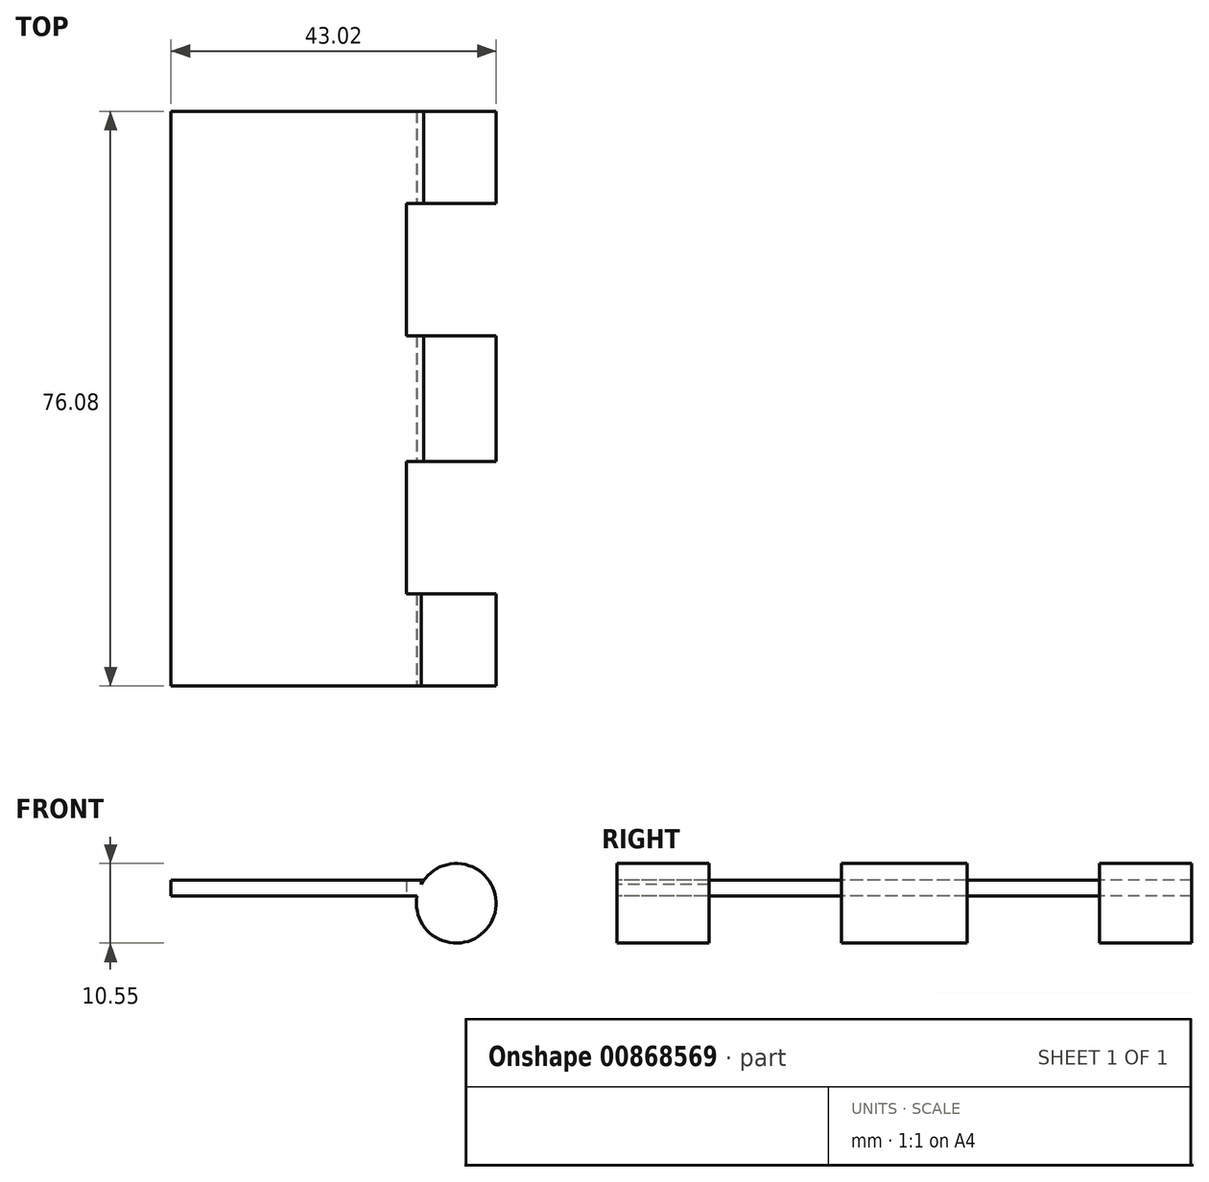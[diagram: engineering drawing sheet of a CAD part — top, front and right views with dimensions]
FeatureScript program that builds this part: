
annotation { "Feature Type Name" : "Feature", "Feature Type Description" : "" }
export const myFeature = defineFeature(function(context is Context, id is Id, definition is map)
    precondition{}
    {
        {
            var Q0;
            Q0=qCreatedBy(makeId("Top.planeOp"),FACE);
            var sketch = newSketch(context, id + "F0", { "sketchPlane" : qUnion([Q0])});
            skLineSegment(sketch, "E0.bottom", {"start": v(15.58, 38.04) * mm, "end": v(-15.58, 38.04) * mm});
            skLineSegment(sketch, "E0.top", {"start": v(15.58, -38.04) * mm, "end": v(-15.58, -38.04) * mm});
            skLineSegment(sketch, "E0.left", {"start": v(15.58, 38.04) * mm, "end": v(15.58, -38.04) * mm});
            skLineSegment(sketch, "E0.right", {"start": v(-15.58, 38.04) * mm, "end": v(-15.58, -38.04) * mm});
            skPoint(sketch, "E0.middle", {"position": v(0, 0) * mm});
            skSolve(sketch);
        }
        {
            var Q0;
            Q0=qSketchRegion(id+"F0",true);
            extrude(context, id + "F1", {"entities" : qUnion([Q0]), "depth" : 2.1 * mm, "offsetDistance" : 25.4 * mm});
        }
        {
            var Q0;
            Q0=makeQuery(id+"F1.opExtrude","SWEPT_FACE",FACE,{"disambiguationData":[OSD([sQuery(id+"F0.wireOp",EDGE,"E0.left")])]});
            var sketch = newSketch(context, id + "F2", { "sketchPlane" : qUnion([Q0])});
            skLineSegment(sketch, "E1.bottom", {"start": v(-25.84, 2.1) * mm, "end": v(-8.32, 2.1) * mm, "construction": true});
            skLineSegment(sketch, "E1.top", {"start": v(-25.84, 0) * mm, "end": v(-8.32, 0) * mm, "construction": true});
            skLineSegment(sketch, "E1.left", {"start": v(-25.84, 2.1) * mm, "end": v(-25.84, 0) * mm, "construction": true});
            skLineSegment(sketch, "E1.right", {"start": v(-8.32, 2.1) * mm, "end": v(-8.32, 0) * mm, "construction": true});
            skLineSegment(sketch, "E2.bottom", {"start": v(8.32, 2.1) * mm, "end": v(25.84, 2.1) * mm, "construction": true});
            skLineSegment(sketch, "E2.top", {"start": v(8.32, 0) * mm, "end": v(25.84, 0) * mm, "construction": true});
            skLineSegment(sketch, "E2.left", {"start": v(8.32, 2.1) * mm, "end": v(8.32, 0) * mm, "construction": true});
            skLineSegment(sketch, "E2.right", {"start": v(25.84, 2.1) * mm, "end": v(25.84, 0) * mm, "construction": true});
            skLineSegment(sketch, "E3.bottom", {"start": v(-38.04, 2.1) * mm, "end": v(-25.84, 2.1) * mm});
            skLineSegment(sketch, "E3.top", {"start": v(-38.04, 0) * mm, "end": v(-25.84, 0) * mm});
            skLineSegment(sketch, "E3.left", {"start": v(-38.04, 2.1) * mm, "end": v(-38.04, 0) * mm});
            skLineSegment(sketch, "E3.right", {"start": v(-25.84, 2.1) * mm, "end": v(-25.84, 0) * mm});
            skLineSegment(sketch, "E4.bottom", {"start": v(-8.32, 2.1) * mm, "end": v(8.32, 2.1) * mm});
            skLineSegment(sketch, "E4.top", {"start": v(-8.32, 0) * mm, "end": v(8.32, 0) * mm});
            skLineSegment(sketch, "E4.left", {"start": v(-8.32, 2.1) * mm, "end": v(-8.32, 0) * mm});
            skLineSegment(sketch, "E4.right", {"start": v(8.32, 2.1) * mm, "end": v(8.32, 0) * mm});
            skLineSegment(sketch, "E5.bottom", {"start": v(25.84, 2.1) * mm, "end": v(38.04, 2.1) * mm});
            skLineSegment(sketch, "E5.top", {"start": v(25.84, 0) * mm, "end": v(38.04, 0) * mm});
            skLineSegment(sketch, "E5.left", {"start": v(25.84, 2.1) * mm, "end": v(25.84, 0) * mm});
            skLineSegment(sketch, "E5.right", {"start": v(38.04, 2.1) * mm, "end": v(38.04, 0) * mm});
            skSolve(sketch);
        }
        {
            var Q0;
            Q0=makeQuery(id+"F2.imprint","IMPRINT",FACE,{"disambiguationData":[TD([[makeQuery(id+"F2.imprint","IMPRINT",EDGE,{"derivedFrom":sQuery(id+"F2.wireOp",EDGE,"E3.bottom")}),1.0]])]});
            var Q1;
            Q1=makeQuery(id+"F2.imprint","IMPRINT",FACE,{"disambiguationData":[TD([[makeQuery(id+"F2.imprint","IMPRINT",EDGE,{"derivedFrom":sQuery(id+"F2.wireOp",EDGE,"E4.bottom")}),1.0]])]});
            var Q2;
            Q2=makeQuery(id+"F2.imprint","IMPRINT",FACE,{"disambiguationData":[TD([[makeQuery(id+"F2.imprint","IMPRINT",EDGE,{"derivedFrom":sQuery(id+"F2.wireOp",EDGE,"E5.bottom")}),1.0]])]});
            extrude(context, id + "F3", {"entities" : qUnion([Q0, Q1, Q2]), "operationType" : NewBodyOperationType.ADD, "depth" : 1.96 * mm, "offsetDistance" : 25.4 * mm});
        }
        {
            var Q0;
            Q0=makeQuery(id+"F3.boolean.opBoolean","MERGE",FACE,{"derivedFrom":[makeQuery(id+"F1.opExtrude","SWEPT_FACE",FACE,{"disambiguationData":[OSD([sQuery(id+"F0.wireOp",EDGE,"E0.top")])]}),makeQuery(id+"F3.opExtrude","SWEPT_FACE",FACE,{"disambiguationData":[OSD([sQuery(id+"F2.wireOp",EDGE,"E3.left")])]})]});
            var sketch = newSketch(context, id + "F4", { "sketchPlane" : qUnion([Q0])});
            skCircle(sketch, "E6", {"center": v(22.17, -0.97) * mm, "radius": 5.27 * mm});
            skPoint(sketch, "E7", {"position": v(22.17, 4.3) * mm});
            skPoint(sketch, "E8", {"position": v(27.44, -0.97) * mm});
            skSolve(sketch);
        }
        {
            var Q0;
            Q0=qSketchRegion(id+"F4",true);
            var Q1;
            Q1=makeQuery(id+"F3.opExtrude","SWEPT_FACE",FACE,{"disambiguationData":[OSD([sQuery(id+"F2.wireOp",EDGE,"E3.right")])]});
            extrude(context, id + "F5", {"entities" : qUnion([Q0]), "operationType" : NewBodyOperationType.ADD, "endBound" : BoundingType.UP_TO_SURFACE, "oppositeDirection" : true, "depth" : 25.4 * mm, "endBoundEntityFace" : qUnion([Q1]), "offsetDistance" : 25.4 * mm});
        }
        {
            var Q0;
            Q0=makeQuery(id+"F3.opExtrude","SWEPT_FACE",FACE,{"disambiguationData":[OSD([sQuery(id+"F2.wireOp",EDGE,"E4.left")])]});
            var sketch = newSketch(context, id + "F6", { "sketchPlane" : qUnion([Q0])});
            skArc(sketch, "E9.0", {"start": v(17, 0) * mm, "mid": v(27.02, -3.03) * mm, "end": v(17.88, 2.1) * mm});
            skLineSegment(sketch, "E10.0", {"start": v(17.54, 2.1) * mm, "end": v(17.54, 0) * mm});
            skLineSegment(sketch, "E11.0", {"start": v(17.88, 2.1) * mm, "end": v(17.54, 2.1) * mm});
            skLineSegment(sketch, "E12.0", {"start": v(17.54, 0) * mm, "end": v(17, 0) * mm});
            skPoint(sketch, "E13.orphan", {"position": v(15.58, 0) * mm});
            skPoint(sketch, "E14.orphan", {"position": v(15.58, 2.1) * mm});
            skSolve(sketch);
        }
        {
            var Q0;
            Q0=qSketchRegion(id+"F6",true);
            var Q1;
            Q1=makeQuery(id+"F3.opExtrude","SWEPT_FACE",FACE,{"disambiguationData":[OSD([sQuery(id+"F2.wireOp",EDGE,"E4.right")])]});
            extrude(context, id + "F7", {"entities" : qUnion([Q0]), "operationType" : NewBodyOperationType.ADD, "endBound" : BoundingType.UP_TO_SURFACE, "oppositeDirection" : true, "depth" : 25.4 * mm, "endBoundEntityFace" : qUnion([Q1]), "offsetDistance" : 25.4 * mm});
        }
        {
            var Q0;
            Q0=makeQuery(id+"F3.opExtrude","SWEPT_FACE",FACE,{"disambiguationData":[OSD([sQuery(id+"F2.wireOp",EDGE,"E5.left")])]});
            var sketch = newSketch(context, id + "F8", { "sketchPlane" : qUnion([Q0])});
            skArc(sketch, "E15.0", {"start": v(17, 0) * mm, "mid": v(27.02, -3.03) * mm, "end": v(17.88, 2.1) * mm});
            skPoint(sketch, "E16.0", {"position": v(17.54, 1.05) * mm});
            skPoint(sketch, "E17.0", {"position": v(17.54, 0) * mm});
            skLineSegment(sketch, "E18.0", {"start": v(17.54, 2.1) * mm, "end": v(17.54, 0) * mm});
            skLineSegment(sketch, "E19.0", {"start": v(17.88, 2.1) * mm, "end": v(17.54, 2.1) * mm});
            skPoint(sketch, "E20.0", {"position": v(16.56, 0) * mm});
            skLineSegment(sketch, "E21.0", {"start": v(17.54, 0) * mm, "end": v(17, 0) * mm});
            skPoint(sketch, "E22.orphan", {"position": v(15.58, 0) * mm});
            skPoint(sketch, "E23.orphan", {"position": v(15.58, 2.1) * mm});
            skSolve(sketch);
        }
        {
            var Q0;
            Q0 = qSketchRegion(id + "F8", true);
            var Q1;
            Q1=makeQuery(id+"F3.boolean.opBoolean","MERGE",FACE,{"derivedFrom":[makeQuery(id+"F1.opExtrude","SWEPT_FACE",FACE,{"disambiguationData":[OSD([sQuery(id+"F0.wireOp",EDGE,"E0.bottom")])]}),makeQuery(id+"F3.opExtrude","SWEPT_FACE",FACE,{"disambiguationData":[OSD([sQuery(id+"F2.wireOp",EDGE,"E5.right")])]})]});
            extrude(context, id + "F9", {"entities" : qUnion([Q0]), "operationType" : NewBodyOperationType.ADD, "endBound" : BoundingType.UP_TO_SURFACE, "oppositeDirection" : true, "depth" : 25.4 * mm, "endBoundEntityFace" : qUnion([Q1]), "offsetDistance" : 25.4 * mm});
        }
    });
